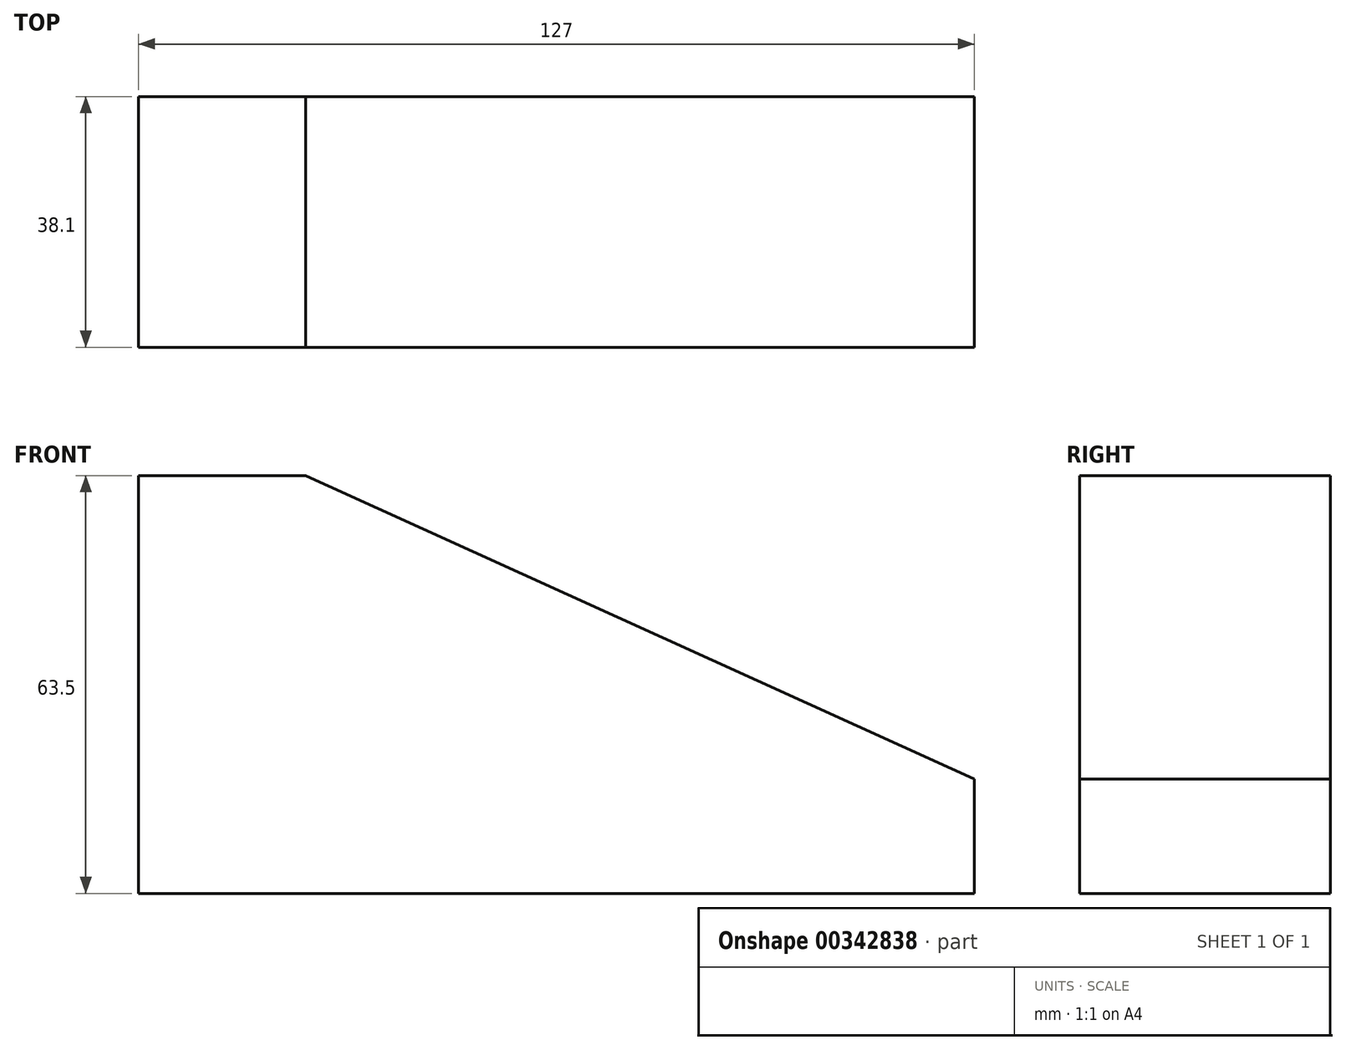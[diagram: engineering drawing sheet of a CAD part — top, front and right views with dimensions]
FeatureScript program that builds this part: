
annotation { "Feature Type Name" : "Feature", "Feature Type Description" : "" }
export const myFeature = defineFeature(function(context is Context, id is Id, definition is map)
    precondition{}
    {
        {
            var Q0;
            Q0=qCreatedBy(makeId("Front.planeOp"),FACE);
            var sketch = newSketch(context, id + "F0", { "sketchPlane" : qUnion([Q0])});
            skLineSegment(sketch, "E0.bottom", {"start": v(-72.5, 0) * mm, "end": v(54.5, 0) * mm});
            skLineSegment(sketch, "E0.top", {"start": v(-72.5, 63.5) * mm, "end": v(-47.1, 63.5) * mm});
            skLineSegment(sketch, "E0.left", {"start": v(-72.5, 0) * mm, "end": v(-72.5, 63.5) * mm});
            skLineSegment(sketch, "E0.right", {"start": v(54.5, 0) * mm, "end": v(54.5, 17.34) * mm});
            skLineSegment(sketch, "E1", {"start": v(-47.1, 63.5) * mm, "end": v(54.5, 17.34) * mm});
            skSolve(sketch);
        }
        {
            var Q0;
            Q0=makeQuery(id+"F0.imprint","IMPRINT",FACE,{"disambiguationData":[TD([[makeQuery(id+"F0.imprint","IMPRINT",EDGE,{"derivedFrom":sQuery(id+"F0.wireOp",EDGE,"E0.bottom")}),1.0]])]});
            extrude(context, id + "F1", {"entities" : qUnion([Q0]), "depth" : 38.1 * mm});
        }
    });
